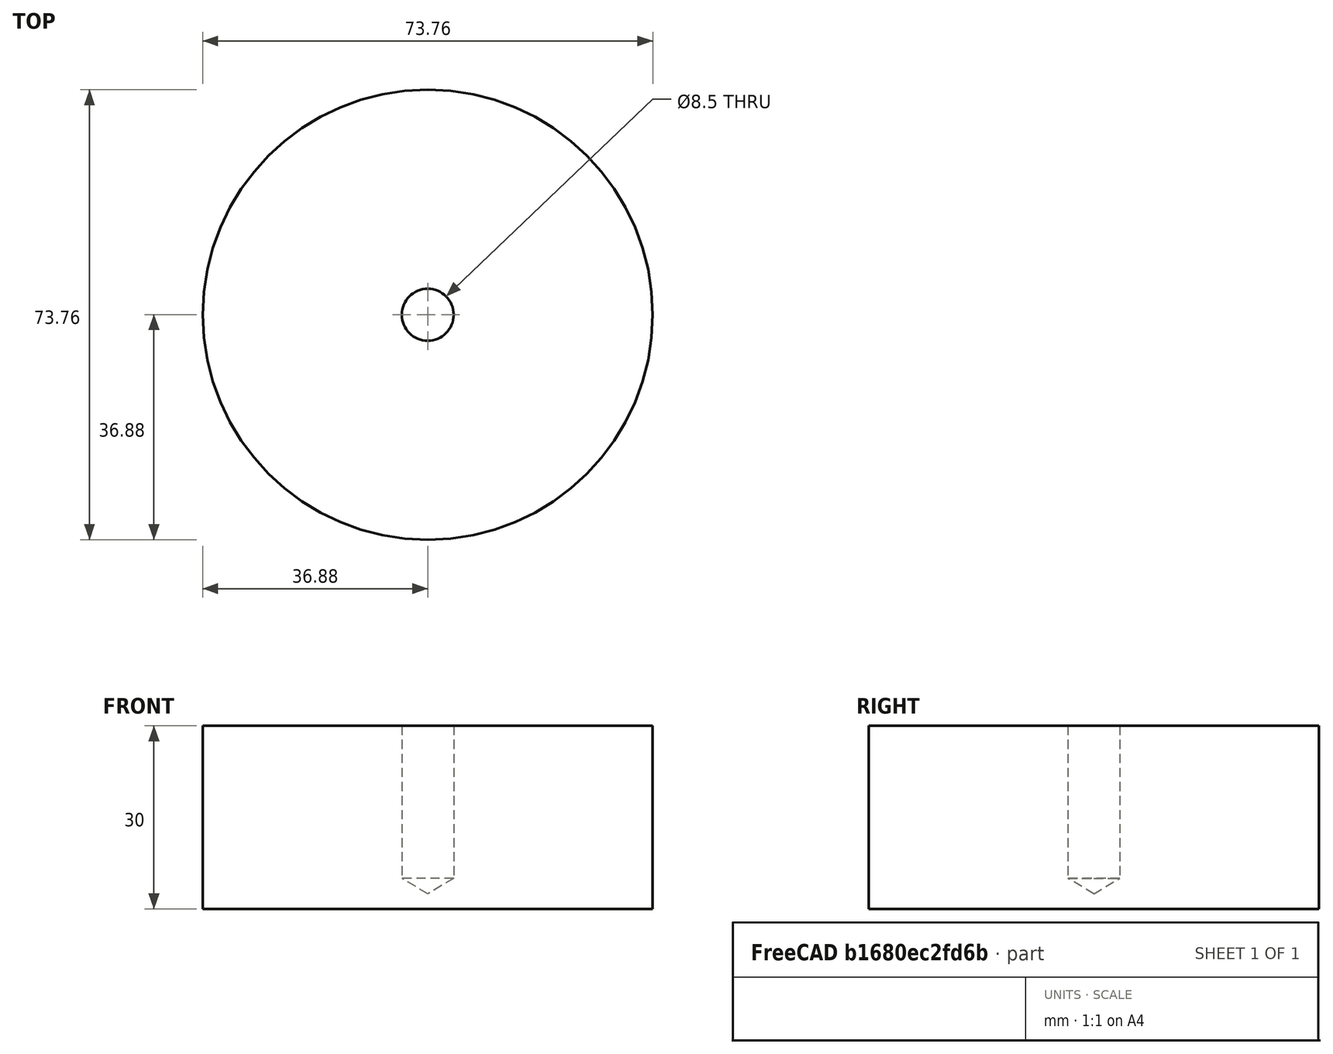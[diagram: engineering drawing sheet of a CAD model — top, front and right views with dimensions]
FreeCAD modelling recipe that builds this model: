
FCSTD DOCUMENT  (FreeCAD 0.19R24291 (Git))
Label: threading 2
License: All rights reserved
LicenseURL: http://en.wikipedia.org/wiki/All_rights_reserved
objects: Sketcher::SketchObject×1, PartDesign::Pad×1, PartDesign::Hole×1, PartDesign::Body×1
note: 6 computed .brp shape members not serialized (recipe doc carries the construction recipe); baked Part::Feature solids carry a one-line shape summary decoded from their .brp

FEATURE [Sketcher::SketchObject] Sketch
  FullyConstrained = false
  MapMode = 5
  Support = -> [XY_Plane]
  sketch-geometry (1):
    g0: Circle CenterX=0 CenterY=0 CenterZ=0 NormalX=0 NormalY=0 NormalZ=1 AngleXU=0 Radius=36.8787
  constraints (1):
    c: Coincident(g0,g-1)
FEATURE [PartDesign::Pad] Pad
  Direction = (1,1,1)
  Length = 30
  Length2 = 100
  Profile = -> Sketch
  Type = 0
FEATURE [PartDesign::Hole] Hole
  BaseFeature = -> Pad
  Depth = 25
  DepthType = 0
  Diameter = 8.5
  DrillForDepth = false
  DrillPoint = 1
  DrillPointAngle = 118
  HoleCutCountersinkAngle = 90
  HoleCutCustomValues = false
  HoleCutDepth = 0
  HoleCutDiameter = 6.1
  HoleCutType = 0
  ModelActualThread = false
  Profile = -> Pad [Face3]
  Tapered = false
  TaperedAngle = 90
  ThreadAngle = 60
  ThreadClass = 0
  ThreadCutOffInner = 0.16238
  ThreadCutOffOuter = 0.32476
  ThreadDirection = 0
  ThreadFit = 0
  ThreadPitch = 1.5
  ThreadSize = 18
  ThreadType = 1
  Threaded = true
FEATURE [PartDesign::Body] Body
  Group = -> [Sketch,Pad,Hole]
  Origin = -> Origin
  Tip = -> Hole
